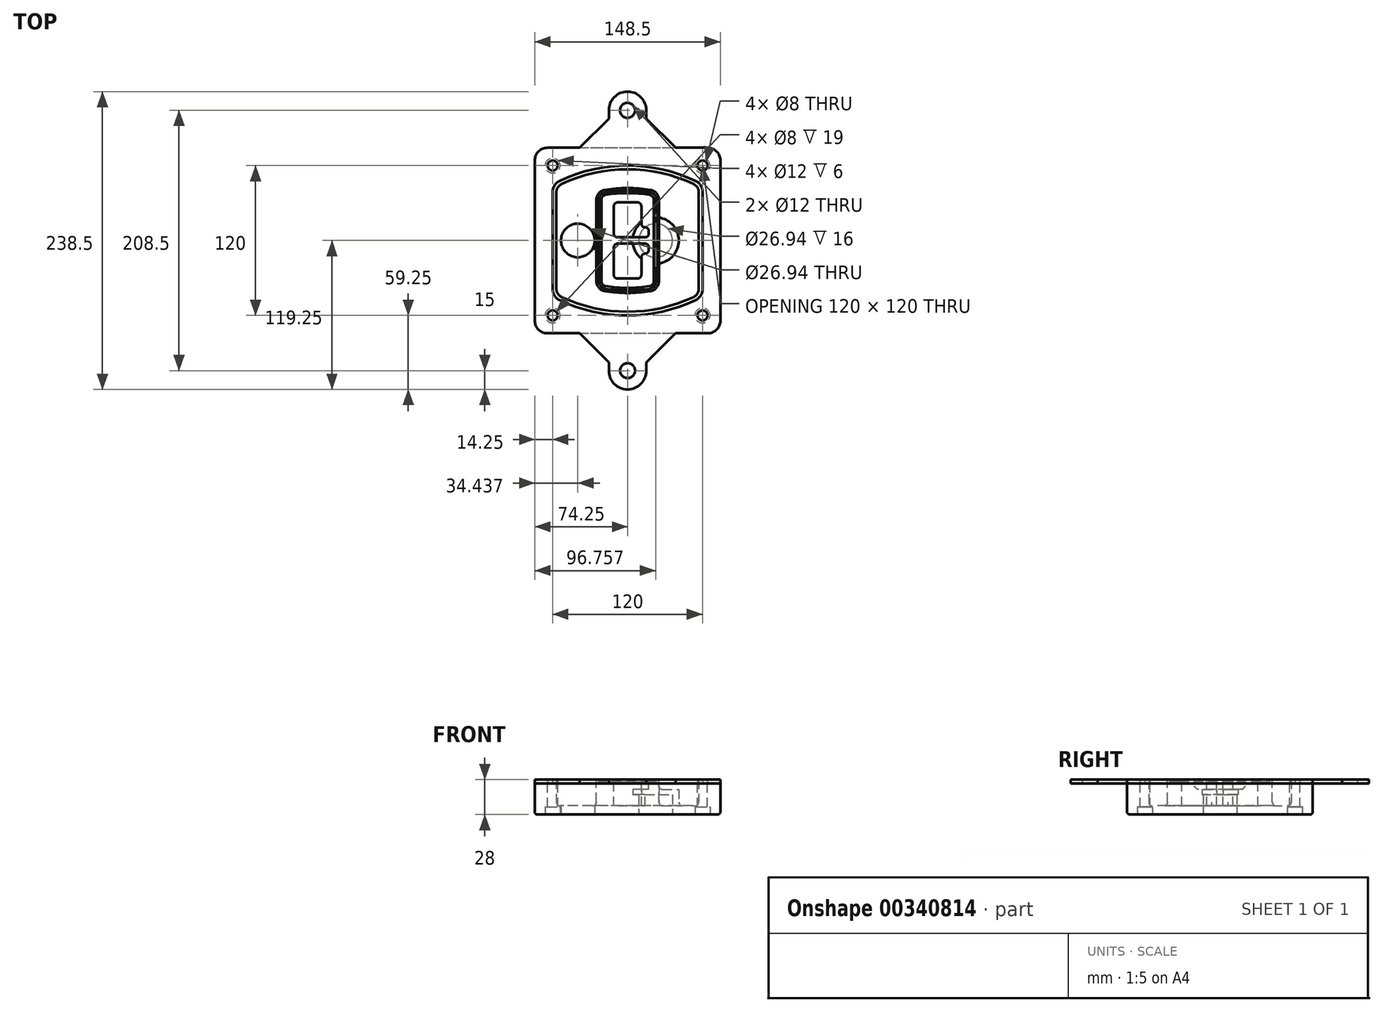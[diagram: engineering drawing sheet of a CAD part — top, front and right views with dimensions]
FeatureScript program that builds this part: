
annotation { "Feature Type Name" : "Feature", "Feature Type Description" : "" }
export const myFeature = defineFeature(function(context is Context, id is Id, definition is map)
    precondition{}
    {
        {
            var Q0;
            Q0=qCreatedBy(makeId("Top.planeOp"),FACE);
            var sketch = newSketch(context, id + "F0", { "sketchPlane" : qUnion([Q0])});
            skPoint(sketch, "E0.rect.middle", {"position": v(0, 0) * mm});
            skLineSegment(sketch, "E1.bottom", {"start": v(-64.25, -74.25) * mm, "end": v(64.25, -74.25) * mm});
            skLineSegment(sketch, "E1.top", {"start": v(-64.25, 74.25) * mm, "end": v(64.25, 74.25) * mm});
            skLineSegment(sketch, "E1.left", {"start": v(-74.25, -64.25) * mm, "end": v(-74.25, 64.25) * mm});
            skLineSegment(sketch, "E1.right", {"start": v(74.25, -64.25) * mm, "end": v(74.25, 64.25) * mm});
            skLineSegment(sketch, "E2", {"start": v(-74.25, 74.25) * mm, "end": v(74.25, -74.25) * mm, "construction": true});
            skLineSegment(sketch, "E3", {"start": v(74.25, 74.25) * mm, "end": v(-74.25, -74.25) * mm, "construction": true});
            skCircle(sketch, "E4", {"center": v(-60, 60) * mm, "radius": 4 * mm});
            skCircle(sketch, "E5", {"center": v(60, 60) * mm, "radius": 4 * mm});
            skCircle(sketch, "E6", {"center": v(60, -60) * mm, "radius": 4 * mm});
            skCircle(sketch, "E7", {"center": v(-60, -60) * mm, "radius": 4 * mm});
            skLineSegment(sketch, "E8", {"start": v(-60, 60) * mm, "end": v(60, 60) * mm, "construction": true});
            skLineSegment(sketch, "E9", {"start": v(60, 60) * mm, "end": v(60, -60) * mm, "construction": true});
            skLineSegment(sketch, "E10", {"start": v(60, -60) * mm, "end": v(-60, -60) * mm, "construction": true});
            skLineSegment(sketch, "E11", {"start": v(-60, -60) * mm, "end": v(-60, 60) * mm, "construction": true});
            skLineSegment(sketch, "E12", {"start": v(-60, 38.83) * mm, "end": v(-60, -38.83) * mm});
            skLineSegment(sketch, "E13", {"start": v(60, 38.83) * mm, "end": v(60, -38.83) * mm});
            skArc(sketch, "E14", {"start": v(54.26, 47.88) * mm, "mid": v(0, 60) * mm, "end": v(-54.26, 47.88) * mm});
            skArc(sketch, "E15", {"start": v(-54.26, -47.88) * mm, "mid": v(0, -60) * mm, "end": v(54.26, -47.88) * mm});
            skLineSegment(sketch, "E16", {"start": v(-60, 0) * mm, "end": v(60, 0) * mm, "construction": true});
            skPoint(sketch, "E17.visualSharp", {"position": v(-60, -45) * mm});
            skArc(sketch, "E17.filletArc", {"start": v(-60, -38.83) * mm, "mid": v(-58.44, -44.2) * mm, "end": v(-54.26, -47.88) * mm});
            skPoint(sketch, "E18.visualSharp", {"position": v(-60, 45) * mm});
            skArc(sketch, "E18.filletArc", {"start": v(-54.26, 47.88) * mm, "mid": v(-58.44, 44.2) * mm, "end": v(-60, 38.83) * mm});
            skPoint(sketch, "E19.visualSharp", {"position": v(60, 45) * mm});
            skArc(sketch, "E19.filletArc", {"start": v(60, 38.83) * mm, "mid": v(58.44, 44.2) * mm, "end": v(54.26, 47.88) * mm});
            skPoint(sketch, "E20.visualSharp", {"position": v(60, -45) * mm});
            skArc(sketch, "E20.filletArc", {"start": v(54.26, -47.88) * mm, "mid": v(58.44, -44.2) * mm, "end": v(60, -38.83) * mm});
            skPoint(sketch, "E21.visualSharp", {"position": v(-74.25, 74.25) * mm});
            skArc(sketch, "E21.filletArc", {"start": v(-64.25, 74.25) * mm, "mid": v(-71.32, 71.32) * mm, "end": v(-74.25, 64.25) * mm});
            skPoint(sketch, "E22.visualSharp", {"position": v(74.25, 74.25) * mm});
            skArc(sketch, "E22.filletArc", {"start": v(74.25, 64.25) * mm, "mid": v(71.32, 71.32) * mm, "end": v(64.25, 74.25) * mm});
            skPoint(sketch, "E23.visualSharp", {"position": v(74.25, -74.25) * mm});
            skArc(sketch, "E23.filletArc", {"start": v(64.25, -74.25) * mm, "mid": v(71.32, -71.32) * mm, "end": v(74.25, -64.25) * mm});
            skPoint(sketch, "E24.visualSharp", {"position": v(-74.25, -74.25) * mm});
            skArc(sketch, "E24.filletArc", {"start": v(-74.25, -64.25) * mm, "mid": v(-71.32, -71.32) * mm, "end": v(-64.25, -74.25) * mm});
            skArc(sketch, "E25.0", {"start": v(57, 38.83) * mm, "mid": v(55.9, 42.58) * mm, "end": v(52.98, 45.17) * mm});
            skLineSegment(sketch, "E25.1", {"start": v(57, 38.83) * mm, "end": v(57, -38.83) * mm});
            skArc(sketch, "E25.2", {"start": v(52.98, -45.17) * mm, "mid": v(55.9, -42.58) * mm, "end": v(57, -38.83) * mm});
            skArc(sketch, "E25.3", {"start": v(-52.98, -45.17) * mm, "mid": v(0, -57) * mm, "end": v(52.98, -45.17) * mm});
            skArc(sketch, "E25.4", {"start": v(-57, -38.83) * mm, "mid": v(-55.9, -42.58) * mm, "end": v(-52.98, -45.17) * mm});
            skArc(sketch, "E25.5", {"start": v(52.98, 45.17) * mm, "mid": v(0, 57) * mm, "end": v(-52.98, 45.17) * mm});
            skLineSegment(sketch, "E25.6", {"start": v(-57, 38.83) * mm, "end": v(-57, -38.83) * mm});
            skArc(sketch, "E25.7", {"start": v(-52.98, 45.17) * mm, "mid": v(-55.9, 42.58) * mm, "end": v(-57, 38.83) * mm});
            skArc(sketch, "E26.0", {"start": v(-55.96, 51.5) * mm, "mid": v(-61.82, 46.33) * mm, "end": v(-64, 38.83) * mm});
            skArc(sketch, "E26.1", {"start": v(55.96, 51.5) * mm, "mid": v(0, 64) * mm, "end": v(-55.96, 51.5) * mm});
            skArc(sketch, "E26.2", {"start": v(64, 38.83) * mm, "mid": v(61.82, 46.33) * mm, "end": v(55.96, 51.5) * mm});
            skLineSegment(sketch, "E26.3", {"start": v(64, 38.83) * mm, "end": v(64, -38.83) * mm});
            skArc(sketch, "E26.4", {"start": v(55.96, -51.5) * mm, "mid": v(61.82, -46.33) * mm, "end": v(64, -38.83) * mm});
            skLineSegment(sketch, "E26.5", {"start": v(-64, 38.83) * mm, "end": v(-64, -38.83) * mm});
            skArc(sketch, "E26.6", {"start": v(-55.96, -51.5) * mm, "mid": v(0, -64) * mm, "end": v(55.96, -51.5) * mm});
            skArc(sketch, "E26.7", {"start": v(-64, -38.83) * mm, "mid": v(-61.82, -46.33) * mm, "end": v(-55.96, -51.5) * mm});
            skSolve(sketch);
        }
        {
            var Q0;
            Q0=makeQuery(id+"F0.imprint","IMPRINT",FACE,{"disambiguationData":[TD([[makeQuery(id+"F0.imprint","IMPRINT",EDGE,{"derivedFrom":sQuery(id+"F0.wireOp",EDGE,"E1.bottom")}),1.0]])]});
            var Q1;
            Q1=makeQuery(id+"F0.imprint","IMPRINT",FACE,{"disambiguationData":[TD([[makeQuery(id+"F0.imprint","IMPRINT",EDGE,{"derivedFrom":sQuery(id+"F0.wireOp",EDGE,"E12")}),1.0]])]});
            var Q2;
            Q2=makeQuery(id+"F0.imprint","IMPRINT",FACE,{"disambiguationData":[TD([[makeQuery(id+"F0.imprint","IMPRINT",EDGE,{"derivedFrom":sQuery(id+"F0.wireOp",EDGE,"E25.0")}),1.0]])]});
            var Q3;
            Q3=makeQuery(id+"F0.imprint","IMPRINT",FACE,{"disambiguationData":[TD([[makeQuery(id+"F0.imprint","IMPRINT",EDGE,{"derivedFrom":sQuery(id+"F0.wireOp",EDGE,"E12")}),-1.0]])]});
            extrude(context, id + "F1", {"entities" : qUnion([Q0, Q1, Q2, Q3]), "oppositeDirection" : true, "depth" : 25 * mm});
        }
        {
            var Q0;
            Q0=makeQuery(id+"F0.imprint","IMPRINT",FACE,{"disambiguationData":[TD([[makeQuery(id+"F0.imprint","IMPRINT",EDGE,{"derivedFrom":sQuery(id+"F0.wireOp",EDGE,"E12")}),1.0]])]});
            extrude(context, id + "F2", {"entities" : qUnion([Q0]), "operationType" : NewBodyOperationType.ADD, "depth" : 3 * mm});
        }
        {
            var Q0;
            Q0=makeQuery(id+"F0.imprint","IMPRINT",FACE,{"disambiguationData":[TD([[makeQuery(id+"F0.imprint","IMPRINT",EDGE,{"derivedFrom":sQuery(id+"F0.wireOp",EDGE,"E25.0")}),1.0]])]});
            extrude(context, id + "F3", {"entities" : qUnion([Q0]), "operationType" : NewBodyOperationType.REMOVE, "oppositeDirection" : true, "depth" : 18 * mm});
        }
        {
            var Q0;
            Q0=makeQuery(id+"F2.opExtrude","CAP_FACE",FACE,{"disambiguationData":[OSD([sQuery(id+"F0.wireOp",EDGE,"E12"),sQuery(id+"F0.wireOp",EDGE,"E13"),sQuery(id+"F0.wireOp",EDGE,"E14"),sQuery(id+"F0.wireOp",EDGE,"E15"),sQuery(id+"F0.wireOp",EDGE,"E17.filletArc"),sQuery(id+"F0.wireOp",EDGE,"E18.filletArc"),sQuery(id+"F0.wireOp",EDGE,"E19.filletArc"),sQuery(id+"F0.wireOp",EDGE,"E20.filletArc"),sQuery(id+"F0.wireOp",EDGE,"E25.0"),sQuery(id+"F0.wireOp",EDGE,"E25.1"),sQuery(id+"F0.wireOp",EDGE,"E25.2"),sQuery(id+"F0.wireOp",EDGE,"E25.3"),sQuery(id+"F0.wireOp",EDGE,"E25.4"),sQuery(id+"F0.wireOp",EDGE,"E25.5"),sQuery(id+"F0.wireOp",EDGE,"E25.6"),sQuery(id+"F0.wireOp",EDGE,"E25.7")])],"isStart":false});
            var sketch = newSketch(context, id + "F4", { "sketchPlane" : qUnion([Q0])});
            skArc(sketch, "E27.0", {"start": v(-18.34, -40.45) * mm, "mid": v(0, -42) * mm, "end": v(18.34, -40.45) * mm});
            skArc(sketch, "E28.0", {"start": v(18.34, 40.45) * mm, "mid": v(0, 42) * mm, "end": v(-18.34, 40.45) * mm});
            skLineSegment(sketch, "E29", {"start": v(-25, 32.57) * mm, "end": v(-25, -32.57) * mm});
            skLineSegment(sketch, "E30", {"start": v(25, 32.57) * mm, "end": v(25, -32.57) * mm});
            skLineSegment(sketch, "E31", {"start": v(-25, 39.1) * mm, "end": v(25, 39.1) * mm, "construction": true});
            skLineSegment(sketch, "E32", {"start": v(-25, -39.1) * mm, "end": v(25, -39.1) * mm, "construction": true});
            skPoint(sketch, "E33.visualSharp", {"position": v(-25, 39.1) * mm});
            skArc(sketch, "E33.filletArc", {"start": v(-18.34, 40.45) * mm, "mid": v(-23.11, 37.73) * mm, "end": v(-25, 32.57) * mm});
            skPoint(sketch, "E34.visualSharp", {"position": v(25, 39.1) * mm});
            skArc(sketch, "E34.filletArc", {"start": v(25, 32.57) * mm, "mid": v(23.11, 37.73) * mm, "end": v(18.34, 40.45) * mm});
            skPoint(sketch, "E35.visualSharp", {"position": v(25, -39.1) * mm});
            skArc(sketch, "E35.filletArc", {"start": v(18.34, -40.45) * mm, "mid": v(23.11, -37.73) * mm, "end": v(25, -32.57) * mm});
            skPoint(sketch, "E36.visualSharp", {"position": v(-25, -39.1) * mm});
            skArc(sketch, "E36.filletArc", {"start": v(-25, -32.57) * mm, "mid": v(-23.11, -37.73) * mm, "end": v(-18.34, -40.45) * mm});
            skArc(sketch, "E37.0", {"start": v(52.98, 45.17) * mm, "mid": v(0, 57) * mm, "end": v(-52.98, 45.17) * mm});
            skArc(sketch, "E37.1", {"start": v(-52.98, 45.17) * mm, "mid": v(-55.9, 42.58) * mm, "end": v(-57, 38.83) * mm});
            skLineSegment(sketch, "E37.2", {"start": v(-57, 38.83) * mm, "end": v(-57, -38.83) * mm});
            skArc(sketch, "E37.3", {"start": v(-57, -38.83) * mm, "mid": v(-55.9, -42.58) * mm, "end": v(-52.98, -45.17) * mm});
            skArc(sketch, "E37.4", {"start": v(-52.98, -45.17) * mm, "mid": v(0, -57) * mm, "end": v(52.98, -45.17) * mm});
            skArc(sketch, "E37.5", {"start": v(52.98, -45.17) * mm, "mid": v(55.9, -42.58) * mm, "end": v(57, -38.83) * mm});
            skLineSegment(sketch, "E37.6", {"start": v(57, 38.83) * mm, "end": v(57, -38.83) * mm});
            skArc(sketch, "E37.7", {"start": v(57, 38.83) * mm, "mid": v(55.9, 42.58) * mm, "end": v(52.98, 45.17) * mm});
            skLineSegment(sketch, "E38.0", {"start": v(23, 32.57) * mm, "end": v(23, -32.57) * mm});
            skArc(sketch, "E38.1", {"start": v(18, -38.48) * mm, "mid": v(21.58, -36.44) * mm, "end": v(23, -32.57) * mm});
            skArc(sketch, "E38.2", {"start": v(-18, -38.48) * mm, "mid": v(0, -40) * mm, "end": v(18, -38.48) * mm});
            skArc(sketch, "E38.3", {"start": v(-23, -32.57) * mm, "mid": v(-21.58, -36.44) * mm, "end": v(-18, -38.48) * mm});
            skLineSegment(sketch, "E38.4", {"start": v(-23, 32.57) * mm, "end": v(-23, -32.57) * mm});
            skArc(sketch, "E38.5", {"start": v(23, 32.57) * mm, "mid": v(21.58, 36.44) * mm, "end": v(18, 38.48) * mm});
            skArc(sketch, "E38.6", {"start": v(-18, 38.48) * mm, "mid": v(-21.58, 36.44) * mm, "end": v(-23, 32.57) * mm});
            skArc(sketch, "E38.7", {"start": v(18, 38.48) * mm, "mid": v(0, 40) * mm, "end": v(-18, 38.48) * mm});
            skArc(sketch, "E39.0", {"start": v(21, 32.57) * mm, "mid": v(20.06, 35.15) * mm, "end": v(17.67, 36.5) * mm});
            skLineSegment(sketch, "E39.1", {"start": v(21, 32.57) * mm, "end": v(21, -32.57) * mm});
            skArc(sketch, "E39.2", {"start": v(17.67, -36.5) * mm, "mid": v(20.06, -35.15) * mm, "end": v(21, -32.57) * mm});
            skArc(sketch, "E39.3", {"start": v(-17.67, -36.5) * mm, "mid": v(0, -38) * mm, "end": v(17.67, -36.5) * mm});
            skArc(sketch, "E39.4", {"start": v(-21, -32.57) * mm, "mid": v(-20.06, -35.15) * mm, "end": v(-17.67, -36.5) * mm});
            skArc(sketch, "E39.5", {"start": v(17.67, 36.5) * mm, "mid": v(0, 38) * mm, "end": v(-17.67, 36.5) * mm});
            skLineSegment(sketch, "E39.6", {"start": v(-21, 32.57) * mm, "end": v(-21, -32.57) * mm});
            skArc(sketch, "E39.7", {"start": v(-17.67, 36.5) * mm, "mid": v(-20.06, 35.15) * mm, "end": v(-21, 32.57) * mm});
            skLineSegment(sketch, "E40", {"start": v(-25, 0) * mm, "end": v(25, 0) * mm, "construction": true});
            skLineSegment(sketch, "E41", {"start": v(-11, 5.5) * mm, "end": v(-11, 27.5) * mm});
            skLineSegment(sketch, "E42", {"start": v(-8, 30.5) * mm, "end": v(8, 30.5) * mm});
            skLineSegment(sketch, "E43", {"start": v(11, 27.5) * mm, "end": v(11, 13.5) * mm});
            skLineSegment(sketch, "E44", {"start": v(14, 10.5) * mm, "end": v(14, 10.5) * mm});
            skLineSegment(sketch, "E45", {"start": v(17, 7.5) * mm, "end": v(17, 5.5) * mm});
            skLineSegment(sketch, "E46", {"start": v(14, 2.5) * mm, "end": v(-8, 2.5) * mm});
            skPoint(sketch, "E47.visualSharp", {"position": v(-11, 30.5) * mm});
            skArc(sketch, "E47.filletArc", {"start": v(-8, 30.5) * mm, "mid": v(-10.12, 29.62) * mm, "end": v(-11, 27.5) * mm});
            skPoint(sketch, "E48.visualSharp", {"position": v(11, 30.5) * mm});
            skArc(sketch, "E48.filletArc", {"start": v(11, 27.5) * mm, "mid": v(10.12, 29.62) * mm, "end": v(8, 30.5) * mm});
            skPoint(sketch, "E49.visualSharp", {"position": v(11, 10.5) * mm});
            skArc(sketch, "E49.filletArc", {"start": v(11, 13.5) * mm, "mid": v(11.88, 11.38) * mm, "end": v(14, 10.5) * mm});
            skPoint(sketch, "E50.visualSharp", {"position": v(17, 10.5) * mm});
            skArc(sketch, "E50.filletArc", {"start": v(17, 7.5) * mm, "mid": v(16.12, 9.62) * mm, "end": v(14, 10.5) * mm});
            skPoint(sketch, "E51.visualSharp", {"position": v(17, 2.5) * mm});
            skArc(sketch, "E51.filletArc", {"start": v(14, 2.5) * mm, "mid": v(16.12, 3.38) * mm, "end": v(17, 5.5) * mm});
            skPoint(sketch, "E52.visualSharp", {"position": v(-11, 2.5) * mm});
            skArc(sketch, "E52.filletArc", {"start": v(-11, 5.5) * mm, "mid": v(-10.12, 3.38) * mm, "end": v(-8, 2.5) * mm});
            skLineSegment(sketch, "E53.0.MirrorCS", {"start": v(14, -2.5) * mm, "end": v(-8, -2.5) * mm});
            skArc(sketch, "E54.0.MirrorCS", {"start": v(-11, -5.5) * mm, "mid": v(-10.12, -3.38) * mm, "end": v(-8, -2.5) * mm});
            skLineSegment(sketch, "E55.0.MirrorCS", {"start": v(-11, -5.5) * mm, "end": v(-11, -27.5) * mm});
            skArc(sketch, "E56.0.MirrorCS", {"start": v(-8, -30.5) * mm, "mid": v(-10.12, -29.62) * mm, "end": v(-11, -27.5) * mm});
            skLineSegment(sketch, "E57.0.MirrorCS", {"start": v(-8, -30.5) * mm, "end": v(8, -30.5) * mm});
            skArc(sketch, "E58.0.MirrorCS", {"start": v(11, -27.5) * mm, "mid": v(10.12, -29.62) * mm, "end": v(8, -30.5) * mm});
            skLineSegment(sketch, "E59.0.MirrorCS", {"start": v(11, -27.5) * mm, "end": v(11, -13.5) * mm});
            skArc(sketch, "E60.0.MirrorCS", {"start": v(11, -13.5) * mm, "mid": v(11.88, -11.38) * mm, "end": v(14, -10.5) * mm});
            skArc(sketch, "E61.0.MirrorCS", {"start": v(17, -7.5) * mm, "mid": v(16.12, -9.62) * mm, "end": v(14, -10.5) * mm});
            skLineSegment(sketch, "E62.0.MirrorCS", {"start": v(17, -7.5) * mm, "end": v(17, -5.5) * mm});
            skArc(sketch, "E63.0.MirrorCS", {"start": v(14, -2.5) * mm, "mid": v(16.12, -3.38) * mm, "end": v(17, -5.5) * mm});
            skSolve(sketch);
        }
        {
            var Q0;
            Q0=makeQuery(id+"F4.imprint","IMPRINT",FACE,{"disambiguationData":[TD([[makeQuery(id+"F4.imprint","IMPRINT",EDGE,{"derivedFrom":sQuery(id+"F4.wireOp",EDGE,"E27.0")}),1.0]])]});
            var Q1;
            Q1=makeQuery(id+"F4.imprint","IMPRINT",FACE,{"disambiguationData":[TD([[makeQuery(id+"F4.imprint","IMPRINT",EDGE,{"derivedFrom":sQuery(id+"F4.wireOp",EDGE,"E38.0")}),-1.0]])]});
            var Q2;
            Q2=makeQuery(id+"F4.imprint","IMPRINT",FACE,{"disambiguationData":[TD([[makeQuery(id+"F4.imprint","IMPRINT",EDGE,{"derivedFrom":sQuery(id+"F4.wireOp",EDGE,"E39.0")}),1.0]])]});
            extrude(context, id + "F5", {"entities" : qUnion([Q0, Q1, Q2]), "operationType" : NewBodyOperationType.ADD, "endBound" : BoundingType.UP_TO_NEXT, "oppositeDirection" : true, "depth" : 25 * mm});
        }
        {
            var Q0;
            Q0=makeQuery(id+"F4.imprint","IMPRINT",FACE,{"disambiguationData":[TD([[makeQuery(id+"F4.imprint","IMPRINT",EDGE,{"derivedFrom":sQuery(id+"F4.wireOp",EDGE,"E38.0")}),-1.0]])]});
            extrude(context, id + "F6", {"entities" : qUnion([Q0]), "operationType" : NewBodyOperationType.REMOVE, "oppositeDirection" : true, "depth" : 2 * mm});
        }
        {
            var Q0;
            Q0=makeQuery(id+"F1.opExtrude","CAP_FACE",FACE,{"disambiguationData":[OSD([sQuery(id+"F0.wireOp",EDGE,"E1.bottom"),sQuery(id+"F0.wireOp",EDGE,"E1.top"),sQuery(id+"F0.wireOp",EDGE,"E1.left"),sQuery(id+"F0.wireOp",EDGE,"E1.right"),sQuery(id+"F0.wireOp",EDGE,"E4"),sQuery(id+"F0.wireOp",EDGE,"E5"),sQuery(id+"F0.wireOp",EDGE,"E6"),sQuery(id+"F0.wireOp",EDGE,"E7"),sQuery(id+"F0.wireOp",EDGE,"E21.filletArc"),sQuery(id+"F0.wireOp",EDGE,"E22.filletArc"),sQuery(id+"F0.wireOp",EDGE,"E23.filletArc"),sQuery(id+"F0.wireOp",EDGE,"E24.filletArc")])],"isStart":false});
            var sketch = newSketch(context, id + "F7", { "sketchPlane" : qUnion([Q0])});
            skCircle(sketch, "E64", {"center": v(22.5, 0) * mm, "radius": 13.47 * mm});
            skCircle(sketch, "E65", {"center": v(-39.81, 0) * mm, "radius": 13.47 * mm});
            skLineSegment(sketch, "E66", {"start": v(74.25, 0) * mm, "end": v(-74.25, 0) * mm});
            skCircle(sketch, "E67", {"center": v(22.5, 0) * mm, "radius": 18.47 * mm});
            skCircle(sketch, "E68", {"center": v(60, -60) * mm, "radius": 6 * mm});
            skCircle(sketch, "E69", {"center": v(-60, -60) * mm, "radius": 6 * mm});
            skCircle(sketch, "E70", {"center": v(-60, 60) * mm, "radius": 6 * mm});
            skCircle(sketch, "E71", {"center": v(60, 60) * mm, "radius": 6 * mm});
            skSolve(sketch);
        }
        {
            var Q0;
            {var subQ1=sQuery(id+"F7.wireOp",EDGE,"E66");var subQ4=sQuery(id+"F7.wireOp",EDGE,"E64");var subQ6=makeQuery(id+"F7.imprint","INTERSECT",VERTEX,{"disambiguationData":[OD(0.0)],"derivedFrom":[subQ4,subQ1]});Q0=makeQuery(id+"F7.imprint","IMPRINT",FACE,{"disambiguationData":[TD([[makeQuery(id+"F7.imprint","IMPRINT",EDGE,{"disambiguationData":[TD([[subQ6,-1.0]])],"derivedFrom":subQ4}),-1.0]])]});}
            var Q1;
            {var subQ0=sQuery(id+"F7.wireOp",EDGE,"E66");var subQ1=sQuery(id+"F7.wireOp",EDGE,"E64");var subQ3=makeQuery(id+"F7.imprint","INTERSECT",VERTEX,{"disambiguationData":[OD(0.0)],"derivedFrom":[subQ1,subQ0]});Q1=makeQuery(id+"F7.imprint","IMPRINT",FACE,{"disambiguationData":[TD([[makeQuery(id+"F7.imprint","IMPRINT",EDGE,{"disambiguationData":[TD([[subQ3,-1.0]])],"derivedFrom":subQ1}),1.0]])]});}
            var Q2;
            {var subQ0=sQuery(id+"F7.wireOp",EDGE,"E66");var subQ1=sQuery(id+"F7.wireOp",EDGE,"E64");var subQ3=makeQuery(id+"F7.imprint","INTERSECT",VERTEX,{"disambiguationData":[OD(0.0)],"derivedFrom":[subQ1,subQ0]});Q2=makeQuery(id+"F7.imprint","IMPRINT",FACE,{"disambiguationData":[TD([[makeQuery(id+"F7.imprint","IMPRINT",EDGE,{"disambiguationData":[TD([[subQ3,1.0]])],"derivedFrom":subQ1}),1.0]])]});}
            var Q3;
            {var subQ1=sQuery(id+"F7.wireOp",EDGE,"E66");var subQ4=sQuery(id+"F7.wireOp",EDGE,"E64");var subQ6=makeQuery(id+"F7.imprint","INTERSECT",VERTEX,{"disambiguationData":[OD(0.0)],"derivedFrom":[subQ4,subQ1]});Q3=makeQuery(id+"F7.imprint","IMPRINT",FACE,{"disambiguationData":[TD([[makeQuery(id+"F7.imprint","IMPRINT",EDGE,{"disambiguationData":[TD([[subQ6,1.0]])],"derivedFrom":subQ4}),-1.0]])]});}
            extrude(context, id + "F8", {"entities" : qUnion([Q0, Q1, Q2, Q3]), "operationType" : NewBodyOperationType.ADD, "oppositeDirection" : true, "depth" : 20 * mm});
        }
        {
            var Q0;
            {var subQ0=sQuery(id+"F7.wireOp",EDGE,"E66");var subQ1=sQuery(id+"F7.wireOp",EDGE,"E64");var subQ3=makeQuery(id+"F7.imprint","INTERSECT",VERTEX,{"disambiguationData":[OD(0.0)],"derivedFrom":[subQ1,subQ0]});Q0=makeQuery(id+"F7.imprint","IMPRINT",FACE,{"disambiguationData":[TD([[makeQuery(id+"F7.imprint","IMPRINT",EDGE,{"disambiguationData":[TD([[subQ3,-1.0]])],"derivedFrom":subQ1}),1.0]])]});}
            var Q1;
            {var subQ0=sQuery(id+"F7.wireOp",EDGE,"E66");var subQ1=sQuery(id+"F7.wireOp",EDGE,"E64");var subQ3=makeQuery(id+"F7.imprint","INTERSECT",VERTEX,{"disambiguationData":[OD(0.0)],"derivedFrom":[subQ1,subQ0]});Q1=makeQuery(id+"F7.imprint","IMPRINT",FACE,{"disambiguationData":[TD([[makeQuery(id+"F7.imprint","IMPRINT",EDGE,{"disambiguationData":[TD([[subQ3,1.0]])],"derivedFrom":subQ1}),1.0]])]});}
            extrude(context, id + "F9", {"entities" : qUnion([Q0, Q1]), "operationType" : NewBodyOperationType.REMOVE, "oppositeDirection" : true, "depth" : 16 * mm});
        }
        {
            var Q0;
            {var subQ0=sQuery(id+"F7.wireOp",EDGE,"E66");var subQ1=sQuery(id+"F7.wireOp",EDGE,"E65");var subQ3=makeQuery(id+"F7.imprint","INTERSECT",VERTEX,{"disambiguationData":[OD(0.0)],"derivedFrom":[subQ1,subQ0]});Q0=makeQuery(id+"F7.imprint","IMPRINT",FACE,{"disambiguationData":[TD([[makeQuery(id+"F7.imprint","IMPRINT",EDGE,{"disambiguationData":[TD([[subQ3,-1.0]])],"derivedFrom":subQ1}),1.0]])]});}
            var Q1;
            {var subQ0=sQuery(id+"F7.wireOp",EDGE,"E66");var subQ1=sQuery(id+"F7.wireOp",EDGE,"E65");var subQ3=makeQuery(id+"F7.imprint","INTERSECT",VERTEX,{"disambiguationData":[OD(0.0)],"derivedFrom":[subQ1,subQ0]});Q1=makeQuery(id+"F7.imprint","IMPRINT",FACE,{"disambiguationData":[TD([[makeQuery(id+"F7.imprint","IMPRINT",EDGE,{"disambiguationData":[TD([[subQ3,1.0]])],"derivedFrom":subQ1}),1.0]])]});}
            extrude(context, id + "F10", {"entities" : qUnion([Q0, Q1]), "operationType" : NewBodyOperationType.REMOVE, "oppositeDirection" : true, "depth" : 25 * mm});
        }
        {
            var Q0;
            Q0=makeQuery(id+"F7.imprint","IMPRINT",FACE,{"disambiguationData":[TD([[makeQuery(id+"F7.imprint","IMPRINT",EDGE,{"derivedFrom":sQuery(id+"F7.wireOp",EDGE,"E68")}),1.0]])]});
            var Q1;
            Q1=makeQuery(id+"F7.imprint","IMPRINT",FACE,{"disambiguationData":[TD([[makeQuery(id+"F7.imprint","IMPRINT",EDGE,{"derivedFrom":makeQuery(id+"F1.opExtrude","CAP_EDGE",EDGE,{"disambiguationData":[OSD([sQuery(id+"F0.wireOp",EDGE,"E5")])],"isStart":false})}),-1.0]])]});
            var Q2;
            Q2=makeQuery(id+"F7.imprint","IMPRINT",FACE,{"disambiguationData":[TD([[makeQuery(id+"F7.imprint","IMPRINT",EDGE,{"derivedFrom":sQuery(id+"F7.wireOp",EDGE,"E69")}),1.0]])]});
            var Q3;
            Q3=makeQuery(id+"F7.imprint","IMPRINT",FACE,{"disambiguationData":[TD([[makeQuery(id+"F7.imprint","IMPRINT",EDGE,{"derivedFrom":makeQuery(id+"F1.opExtrude","CAP_EDGE",EDGE,{"disambiguationData":[OSD([sQuery(id+"F0.wireOp",EDGE,"E4")])],"isStart":false})}),-1.0]])]});
            var Q4;
            Q4=makeQuery(id+"F7.imprint","IMPRINT",FACE,{"disambiguationData":[TD([[makeQuery(id+"F7.imprint","IMPRINT",EDGE,{"derivedFrom":sQuery(id+"F7.wireOp",EDGE,"E70")}),1.0]])]});
            var Q5;
            Q5=makeQuery(id+"F7.imprint","IMPRINT",FACE,{"disambiguationData":[TD([[makeQuery(id+"F7.imprint","IMPRINT",EDGE,{"derivedFrom":makeQuery(id+"F1.opExtrude","CAP_EDGE",EDGE,{"disambiguationData":[OSD([sQuery(id+"F0.wireOp",EDGE,"E7")])],"isStart":false})}),-1.0]])]});
            var Q6;
            Q6=makeQuery(id+"F7.imprint","IMPRINT",FACE,{"disambiguationData":[TD([[makeQuery(id+"F7.imprint","IMPRINT",EDGE,{"derivedFrom":sQuery(id+"F7.wireOp",EDGE,"E71")}),1.0]])]});
            var Q7;
            Q7=makeQuery(id+"F7.imprint","IMPRINT",FACE,{"disambiguationData":[TD([[makeQuery(id+"F7.imprint","IMPRINT",EDGE,{"derivedFrom":makeQuery(id+"F1.opExtrude","CAP_EDGE",EDGE,{"disambiguationData":[OSD([sQuery(id+"F0.wireOp",EDGE,"E6")])],"isStart":false})}),-1.0]])]});
            extrude(context, id + "F11", {"entities" : qUnion([Q0, Q1, Q2, Q3, Q4, Q5, Q6, Q7]), "operationType" : NewBodyOperationType.REMOVE, "oppositeDirection" : true, "depth" : 6 * mm});
        }
        {
            var Q0;
            Q0=makeQuery(id+"F9.boolean.opBoolean","COPY",FACE,{"derivedFrom":makeQuery(id+"F9.opExtrude","CAP_FACE",FACE,{"disambiguationData":[OSD([sQuery(id+"F7.wireOp",EDGE,"E64")])],"isStart":false})});
            var sketch = newSketch(context, id + "F12", { "sketchPlane" : qUnion([Q0])});
            skArc(sketch, "E72.0", {"start": v(11, 14.45) * mm, "mid": v(6.45, 9.13) * mm, "end": v(4.2, 2.5) * mm});
            skArc(sketch, "E72.1", {"start": v(4.2, -2.5) * mm, "mid": v(6.45, -9.13) * mm, "end": v(11, -14.45) * mm});
            skLineSegment(sketch, "E73", {"start": v(4.2, -2.5) * mm, "end": v(14, -2.5) * mm});
            skLineSegment(sketch, "E74.0", {"start": v(14, 2.5) * mm, "end": v(4.2, 2.5) * mm});
            skArc(sketch, "E74.1", {"start": v(14, 2.5) * mm, "mid": v(16.12, 3.38) * mm, "end": v(17, 5.5) * mm});
            skLineSegment(sketch, "E74.2", {"start": v(17, 7.5) * mm, "end": v(17, 5.5) * mm});
            skArc(sketch, "E74.3", {"start": v(17, 7.5) * mm, "mid": v(16.12, 9.62) * mm, "end": v(14, 10.5) * mm});
            skArc(sketch, "E74.4", {"start": v(11, 13.5) * mm, "mid": v(11.88, 11.38) * mm, "end": v(14, 10.5) * mm});
            skLineSegment(sketch, "E74.5", {"start": v(11, 14.45) * mm, "end": v(11, 13.5) * mm});
            skLineSegment(sketch, "E74.7", {"start": v(14, -2.5) * mm, "end": v(4.2, -2.5) * mm});
            skArc(sketch, "E74.8", {"start": v(14, -2.5) * mm, "mid": v(16.12, -3.38) * mm, "end": v(17, -5.5) * mm});
            skLineSegment(sketch, "E74.9", {"start": v(17, -7.5) * mm, "end": v(17, -5.5) * mm});
            skArc(sketch, "E74.10", {"start": v(17, -7.5) * mm, "mid": v(16.12, -9.62) * mm, "end": v(14, -10.5) * mm});
            skArc(sketch, "E74.11", {"start": v(11, -13.5) * mm, "mid": v(11.88, -11.38) * mm, "end": v(14, -10.5) * mm});
            skLineSegment(sketch, "E74.12", {"start": v(11, -14.45) * mm, "end": v(11, -13.5) * mm});
            skPoint(sketch, "E75.orphan", {"position": v(11, -27.5) * mm});
            skPoint(sketch, "E76.orphan", {"position": v(-8, -2.5) * mm});
            skPoint(sketch, "E77.orphan", {"position": v(-8, 2.5) * mm});
            skPoint(sketch, "E78.orphan", {"position": v(11, 27.5) * mm});
            skSolve(sketch);
        }
        {
            var Q0;
            {var subQ7=sQuery(id+"F12.wireOp",EDGE,"E72.0");var subQ14=sQuery(id+"F12.wireOp",EDGE,"E72.1");var subQ16=sQuery(id+"F12.wireOp",EDGE,"E74.1");var subQ18=sQuery(id+"F12.wireOp",EDGE,"E74.8");Q0=qUnion([makeQuery(id+"F12.imprint","IMPRINT",FACE,{"disambiguationData":[TD([[makeQuery(id+"F12.imprint","IMPRINT",EDGE,{"derivedFrom":subQ7}),1.0]])]}),makeQuery(id+"F12.imprint","IMPRINT",FACE,{"disambiguationData":[TD([[makeQuery(id+"F12.imprint","IMPRINT",EDGE,{"derivedFrom":subQ14}),1.0]])]}),makeQuery(id+"F12.imprint","IMPRINT",FACE,{"disambiguationData":[TD([[makeQuery(id+"F12.imprint","IMPRINT",EDGE,{"derivedFrom":subQ16}),1.0]])]}),makeQuery(id+"F12.imprint","IMPRINT",FACE,{"disambiguationData":[TD([[makeQuery(id+"F12.imprint","IMPRINT",EDGE,{"derivedFrom":subQ18}),-1.0]])]})]);}
            var Q1;
            Q1=makeQuery(id+"F5.boolean.opBoolean","SPLIT",FACE,{"disambiguationData":[TD([makeQuery(id+"F5.opExtrude","SWEPT_FACE",FACE,{"disambiguationData":[OSD([sQuery(id+"F4.wireOp",EDGE,"E41")])]})])],"derivedFrom":makeQuery(id+"F3.boolean.opBoolean","COPY",FACE,{"derivedFrom":makeQuery(id+"F3.opExtrude","CAP_FACE",FACE,{"disambiguationData":[OSD([sQuery(id+"F0.wireOp",EDGE,"E25.0"),sQuery(id+"F0.wireOp",EDGE,"E25.1"),sQuery(id+"F0.wireOp",EDGE,"E25.2"),sQuery(id+"F0.wireOp",EDGE,"E25.3"),sQuery(id+"F0.wireOp",EDGE,"E25.4"),sQuery(id+"F0.wireOp",EDGE,"E25.5"),sQuery(id+"F0.wireOp",EDGE,"E25.6"),sQuery(id+"F0.wireOp",EDGE,"E25.7")])],"isStart":false})})});
            extrude(context, id + "F13", {"entities" : qUnion([Q0]), "operationType" : NewBodyOperationType.REMOVE, "endBound" : BoundingType.UP_TO_SURFACE, "endBoundEntityFace" : qUnion([Q1]), "depth" : 25 * mm});
        }
        {
            var Q0;
            Q0=makeQuery(id+"F3.boolean.opBoolean","COPY",EDGE,{"derivedFrom":makeQuery(id+"F3.opExtrude","CAP_EDGE",EDGE,{"disambiguationData":[OSD([sQuery(id+"F0.wireOp",EDGE,"E25.6")])],"isStart":false})});
            var Q1;
            Q1=makeQuery(id+"F8.boolean.opBoolean","INTERSECT",EDGE,{"derivedFrom":[makeQuery(id+"F5.opExtrude","SWEPT_FACE",FACE,{"disambiguationData":[OSD([sQuery(id+"F4.wireOp",EDGE,"E30")])]}),makeQuery(id+"F8.opExtrude","CAP_FACE",FACE,{"disambiguationData":[OSD([sQuery(id+"F7.wireOp",EDGE,"E67")])],"isStart":false})]});
            var Q2;
            Q2=makeQuery(id+"F8.boolean.opBoolean","INTERSECT",EDGE,{"disambiguationData":[OD(1.0)],"derivedFrom":[makeQuery(id+"F5.opExtrude","SWEPT_FACE",FACE,{"disambiguationData":[OSD([sQuery(id+"F4.wireOp",EDGE,"E30")])]}),makeQuery(id+"F8.opExtrude","SWEPT_FACE",FACE,{"disambiguationData":[OSD([sQuery(id+"F7.wireOp",EDGE,"E67")])]})]});
            var Q3;
            {var subQ0=sQuery(id+"F4.wireOp",EDGE,"E30");Q3=makeQuery(id+"F8.boolean.opBoolean","SPLIT",EDGE,{"disambiguationData":[TD([makeQuery(id+"F5.opExtrude","SWEPT_FACE",FACE,{"disambiguationData":[OSD([sQuery(id+"F4.wireOp",EDGE,"E35.filletArc")])]})])],"derivedFrom":makeQuery(id+"F5.opExtrude","CAP_EDGE",EDGE,{"disambiguationData":[OSD([subQ0])],"isStart":false})});}
            var Q4;
            {var subQ0=sQuery(id+"F0.wireOp",EDGE,"E25.7");var subQ1=sQuery(id+"F0.wireOp",EDGE,"E25.1");var subQ2=sQuery(id+"F0.wireOp",EDGE,"E25.6");var subQ3=sQuery(id+"F0.wireOp",EDGE,"E25.5");var subQ4=sQuery(id+"F0.wireOp",EDGE,"E25.4");var subQ5=sQuery(id+"F0.wireOp",EDGE,"E25.0");var subQ6=sQuery(id+"F0.wireOp",EDGE,"E25.2");var subQ7=sQuery(id+"F0.wireOp",EDGE,"E25.3");Q4=makeQuery(id+"F8.boolean.opBoolean","INTERSECT",EDGE,{"derivedFrom":[makeQuery(id+"F5.boolean.opBoolean","SPLIT",FACE,{"disambiguationData":[TD([makeQuery(id+"F2.opExtrude","SWEPT_FACE",FACE,{"disambiguationData":[OSD([subQ5])]})])],"derivedFrom":makeQuery(id+"F3.boolean.opBoolean","COPY",FACE,{"derivedFrom":makeQuery(id+"F3.opExtrude","CAP_FACE",FACE,{"disambiguationData":[OSD([subQ5,subQ1,subQ6,subQ7,subQ4,subQ3,subQ2,subQ0])],"isStart":false})})}),makeQuery(id+"F8.opExtrude","SWEPT_FACE",FACE,{"disambiguationData":[OSD([sQuery(id+"F7.wireOp",EDGE,"E67")])]})]});}
            var Q5;
            Q5=makeQuery(id+"F8.boolean.opBoolean","INTERSECT",EDGE,{"disambiguationData":[OD(0.0)],"derivedFrom":[makeQuery(id+"F5.opExtrude","SWEPT_FACE",FACE,{"disambiguationData":[OSD([sQuery(id+"F4.wireOp",EDGE,"E30")])]}),makeQuery(id+"F8.opExtrude","SWEPT_FACE",FACE,{"disambiguationData":[OSD([sQuery(id+"F7.wireOp",EDGE,"E67")])]})]});
            fillet(context, id + "F14", {"entities" : qUnion([Q0, Q1, Q2, Q3, Q4, Q5]), "radius" : 3 * mm, "tangentPropagation" : true, "allowEdgeOverflow" : false});
        }
        {
            var Q0;
            Q0=makeQuery(id+"F1.opExtrude","CAP_EDGE",EDGE,{"disambiguationData":[OSD([sQuery(id+"F0.wireOp",EDGE,"E1.bottom")])],"isStart":false});
            fillet(context, id + "F15", {"entities" : qUnion([Q0]), "radius" : 2 * mm, "tangentPropagation" : true, "allowEdgeOverflow" : false});
        }
        {
            var Q0;
            {var subQ0=sQuery(id+"F0.wireOp",EDGE,"E21.filletArc");var subQ1=sQuery(id+"F0.wireOp",EDGE,"E7");var subQ2=sQuery(id+"F0.wireOp",EDGE,"E6");var subQ3=sQuery(id+"F0.wireOp",EDGE,"E5");var subQ4=sQuery(id+"F0.wireOp",EDGE,"E4");var subQ5=sQuery(id+"F0.wireOp",EDGE,"E22.filletArc");var subQ6=sQuery(id+"F0.wireOp",EDGE,"E1.bottom");var subQ7=sQuery(id+"F0.wireOp",EDGE,"E1.right");var subQ8=sQuery(id+"F0.wireOp",EDGE,"E1.top");var subQ9=sQuery(id+"F0.wireOp",EDGE,"E1.left");var subQ10=sQuery(id+"F0.wireOp",EDGE,"E23.filletArc");var subQ11=sQuery(id+"F0.wireOp",EDGE,"E24.filletArc");Q0=makeQuery(id+"F2.boolean.opBoolean","SPLIT",FACE,{"disambiguationData":[TD([makeQuery(id+"F1.opExtrude","SWEPT_FACE",FACE,{"disambiguationData":[OSD([subQ6])]})])],"derivedFrom":makeQuery(id+"F1.opExtrude","CAP_FACE",FACE,{"disambiguationData":[OSD([subQ6,subQ8,subQ9,subQ7,subQ4,subQ3,subQ2,subQ1,subQ0,subQ5,subQ10,subQ11])],"isStart":true})});}
            var sketch = newSketch(context, id + "F16", { "sketchPlane" : qUnion([Q0])});
            skLineSegment(sketch, "E79.0", {"start": v(-64.25, 74.25) * mm, "end": v(64.25, 74.25) * mm});
            skArc(sketch, "E79.1", {"start": v(-64.25, 74.25) * mm, "mid": v(-71.32, 71.32) * mm, "end": v(-74.25, 64.25) * mm});
            skLineSegment(sketch, "E79.2", {"start": v(-74.25, -64.25) * mm, "end": v(-74.25, 64.25) * mm});
            skArc(sketch, "E79.3", {"start": v(-74.25, -64.25) * mm, "mid": v(-71.32, -71.32) * mm, "end": v(-64.25, -74.25) * mm});
            skLineSegment(sketch, "E79.4", {"start": v(-64.25, -74.25) * mm, "end": v(64.25, -74.25) * mm});
            skArc(sketch, "E79.5", {"start": v(64.25, -74.25) * mm, "mid": v(71.32, -71.32) * mm, "end": v(74.25, -64.25) * mm});
            skLineSegment(sketch, "E79.6", {"start": v(74.25, -64.25) * mm, "end": v(74.25, 64.25) * mm});
            skArc(sketch, "E79.7", {"start": v(74.25, 64.25) * mm, "mid": v(71.32, 71.32) * mm, "end": v(64.25, 74.25) * mm});
            skCircle(sketch, "E79.8", {"center": v(60, 60) * mm, "radius": 4 * mm});
            skCircle(sketch, "E79.9", {"center": v(-60, 60) * mm, "radius": 4 * mm});
            skCircle(sketch, "E79.10", {"center": v(-60, -60) * mm, "radius": 4 * mm});
            skCircle(sketch, "E79.11", {"center": v(60, -60) * mm, "radius": 4 * mm});
            skLineSegment(sketch, "E79.12", {"start": v(60, 38.83) * mm, "end": v(60, -38.83) * mm});
            skArc(sketch, "E79.13", {"start": v(54.26, 47.88) * mm, "mid": v(0, 60) * mm, "end": v(-54.26, 47.88) * mm});
            skArc(sketch, "E79.14", {"start": v(-54.26, 47.88) * mm, "mid": v(-58.44, 44.2) * mm, "end": v(-60, 38.83) * mm});
            skLineSegment(sketch, "E79.15", {"start": v(-60, 38.83) * mm, "end": v(-60, -38.83) * mm});
            skArc(sketch, "E79.16", {"start": v(-60, -38.83) * mm, "mid": v(-58.44, -44.2) * mm, "end": v(-54.26, -47.88) * mm});
            skArc(sketch, "E79.17", {"start": v(-54.26, -47.88) * mm, "mid": v(0, -60) * mm, "end": v(54.26, -47.88) * mm});
            skArc(sketch, "E79.18", {"start": v(54.26, -47.88) * mm, "mid": v(58.44, -44.2) * mm, "end": v(60, -38.83) * mm});
            skArc(sketch, "E79.19", {"start": v(60, 38.83) * mm, "mid": v(58.44, 44.2) * mm, "end": v(54.26, 47.88) * mm});
            skLineSegment(sketch, "E80", {"start": v(0, 74.25) * mm, "end": v(0, 104.25) * mm, "construction": true});
            skCircle(sketch, "E81", {"center": v(0, 104.25) * mm, "radius": 6 * mm});
            skLineSegment(sketch, "E82", {"start": v(-38.49, 74.25) * mm, "end": v(-15, 97.74) * mm});
            skLineSegment(sketch, "E83", {"start": v(-15, 97.74) * mm, "end": v(-15, 104.25) * mm});
            skLineSegment(sketch, "E84", {"start": v(38.49, 74.25) * mm, "end": v(15, 97.74) * mm});
            skLineSegment(sketch, "E85", {"start": v(15, 97.74) * mm, "end": v(15, 104.25) * mm});
            skArc(sketch, "E86", {"start": v(15, 104.25) * mm, "mid": v(0, 119.25) * mm, "end": v(-15, 104.25) * mm});
            skLineSegment(sketch, "E87.MirrorCS", {"start": v(64.25, -74.25) * mm, "end": v(-64.25, -74.25) * mm});
            skArc(sketch, "E88.MirrorCS", {"start": v(-15, 104.25) * mm, "mid": v(0, 119.25) * mm, "end": v(15, 104.25) * mm});
            skLineSegment(sketch, "E89", {"start": v(-74.25, 0) * mm, "end": v(74.25, 0) * mm, "construction": true});
            skLineSegment(sketch, "E90.MirrorCS", {"start": v(-38.49, -74.25) * mm, "end": v(-15, -97.74) * mm});
            skLineSegment(sketch, "E91.MirrorCS", {"start": v(0, -74.25) * mm, "end": v(0, -104.25) * mm, "construction": true});
            skLineSegment(sketch, "E92.MirrorCS", {"start": v(38.49, -74.25) * mm, "end": v(15, -97.74) * mm});
            skArc(sketch, "E93.MirrorCS", {"start": v(15, -104.25) * mm, "mid": v(0, -119.25) * mm, "end": v(-15, -104.25) * mm});
            skLineSegment(sketch, "E94.MirrorCS", {"start": v(-15, -97.74) * mm, "end": v(-15, -104.25) * mm});
            skLineSegment(sketch, "E95.MirrorCS", {"start": v(15, -97.74) * mm, "end": v(15, -104.25) * mm});
            skCircle(sketch, "E96.MirrorC", {"center": v(0, -104.25) * mm, "radius": 6 * mm});
            skSolve(sketch);
        }
        {
            var Q0;
            Q0 = qSketchRegion(id + "F16", true);
            var Q1;
            Q1=makeQuery(id+"F2.opExtrude","CAP_FACE",FACE,{"disambiguationData":[OSD([sQuery(id+"F0.wireOp",EDGE,"E12"),sQuery(id+"F0.wireOp",EDGE,"E13"),sQuery(id+"F0.wireOp",EDGE,"E14"),sQuery(id+"F0.wireOp",EDGE,"E15"),sQuery(id+"F0.wireOp",EDGE,"E17.filletArc"),sQuery(id+"F0.wireOp",EDGE,"E18.filletArc"),sQuery(id+"F0.wireOp",EDGE,"E19.filletArc"),sQuery(id+"F0.wireOp",EDGE,"E20.filletArc"),sQuery(id+"F0.wireOp",EDGE,"E25.0"),sQuery(id+"F0.wireOp",EDGE,"E25.1"),sQuery(id+"F0.wireOp",EDGE,"E25.2"),sQuery(id+"F0.wireOp",EDGE,"E25.3"),sQuery(id+"F0.wireOp",EDGE,"E25.4"),sQuery(id+"F0.wireOp",EDGE,"E25.5"),sQuery(id+"F0.wireOp",EDGE,"E25.6"),sQuery(id+"F0.wireOp",EDGE,"E25.7")])],"isStart":false});
            extrude(context, id + "F17", {"entities" : qUnion([Q0]), "endBound" : BoundingType.UP_TO_SURFACE, "endBoundEntityFace" : qUnion([Q1]), "depth" : 25 * mm});
        }
    });
